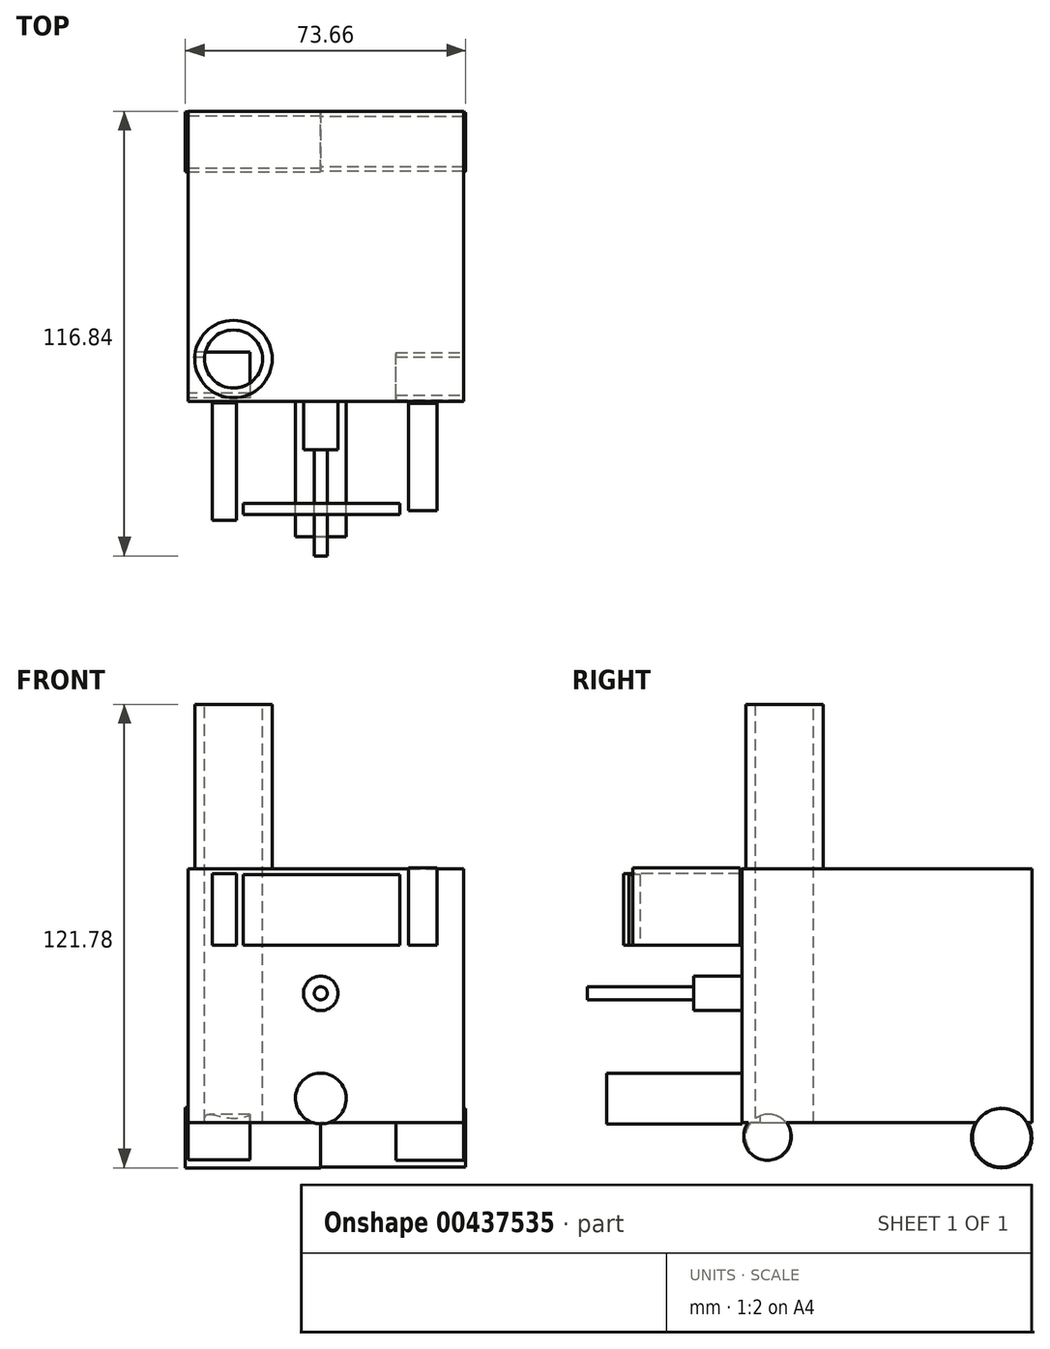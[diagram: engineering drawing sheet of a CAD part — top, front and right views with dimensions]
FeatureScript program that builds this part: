
annotation { "Feature Type Name" : "Feature", "Feature Type Description" : "" }
export const myFeature = defineFeature(function(context is Context, id is Id, definition is map)
    precondition{}
    {
        {
            var Q0;
            Q0=qCreatedBy(makeId("Front.planeOp"),FACE);
            var sketch = newSketch(context, id + "F0", { "sketchPlane" : qUnion([Q0])});
            skLineSegment(sketch, "E0.bottom", {"start": v(-34.88, -34.01) * mm, "end": v(37.54, -34.01) * mm});
            skLineSegment(sketch, "E0.top", {"start": v(-34.88, 32.75) * mm, "end": v(37.54, 32.75) * mm});
            skLineSegment(sketch, "E0.left", {"start": v(-34.88, -34.01) * mm, "end": v(-34.88, 32.75) * mm});
            skLineSegment(sketch, "E0.right", {"start": v(37.54, -34.01) * mm, "end": v(37.54, 32.75) * mm});
            skSolve(sketch);
        }
        {
            var Q0;
            Q0 = qSketchRegion(id + "F0", true);
            extrude(context, id + "F1", {"entities" : qUnion([Q0]), "depth" : 76.2 * mm});
        }
        {
            var Q0;
            Q0=makeQuery(id+"F1.opExtrude","SWEPT_FACE",FACE,{"disambiguationData":[OSD([sQuery(id+"F0.wireOp",EDGE,"E0.top")])]});
            var sketch = newSketch(context, id + "F2", { "sketchPlane" : qUnion([Q0])});
            skCircle(sketch, "E1", {"center": v(-22.93, -65.1) * mm, "radius": 10.17 * mm});
            skSolve(sketch);
        }
        {
            var Q0;
            Q0 = qSketchRegion(id + "F2", true);
            extrude(context, id + "F3", {"entities" : qUnion([Q0]), "operationType" : NewBodyOperationType.ADD, "depth" : 43.18 * mm});
        }
        {
            var Q0;
            Q0=makeQuery(id+"F1.opExtrude","CAP_FACE",FACE,{"disambiguationData":[OSD([sQuery(id+"F0.wireOp",EDGE,"E0.bottom"),sQuery(id+"F0.wireOp",EDGE,"E0.top"),sQuery(id+"F0.wireOp",EDGE,"E0.left"),sQuery(id+"F0.wireOp",EDGE,"E0.right")])],"isStart":false});
            var sketch = newSketch(context, id + "F4", { "sketchPlane" : qUnion([Q0])});
            skCircle(sketch, "E2", {"center": v(0, -27.64) * mm, "radius": 6.67 * mm});
            skSolve(sketch);
        }
        {
            var Q0;
            Q0 = qSketchRegion(id + "F4", true);
            extrude(context, id + "F5", {"entities" : qUnion([Q0]), "operationType" : NewBodyOperationType.ADD, "depth" : 35.56 * mm});
        }
        {
            var Q0;
            Q0=qCreatedBy(makeId("Right.planeOp"),FACE);
            var sketch = newSketch(context, id + "F6", { "sketchPlane" : qUnion([Q0])});
            skCircle(sketch, "E3", {"center": v(-8.03, -37.95) * mm, "radius": 7.71 * mm});
            skSolve(sketch);
        }
        {
            var Q0;
            Q0 = qSketchRegion(id + "F6", true);
            extrude(context, id + "F7", {"entities" : qUnion([Q0]), "operationType" : NewBodyOperationType.ADD, "depth" : 38.1 * mm});
        }
        {
            var Q0;
            Q0=makeQuery(id+"F7.opExtrude","CAP_FACE",FACE,{"disambiguationData":[OSD([sQuery(id+"F6.wireOp",EDGE,"E3")])],"isStart":true});
            var sketch = newSketch(context, id + "F8", { "sketchPlane" : qUnion([Q0])});
            skCircle(sketch, "E4", {"center": v(8.03, -37.95) * mm, "radius": 7.9 * mm});
            skSolve(sketch);
        }
        {
            var Q0;
            Q0 = qSketchRegion(id + "F8", true);
            extrude(context, id + "F9", {"entities" : qUnion([Q0]), "operationType" : NewBodyOperationType.ADD, "depth" : 35.56 * mm});
        }
        {
            var Q0;
            Q0=makeQuery(id+"F1.opExtrude","SWEPT_FACE",FACE,{"disambiguationData":[OSD([sQuery(id+"F0.wireOp",EDGE,"E0.right")])]});
            var sketch = newSketch(context, id + "F10", { "sketchPlane" : qUnion([Q0])});
            skCircle(sketch, "E5", {"center": v(-69.6, -37.64) * mm, "radius": 6.22 * mm});
            skSolve(sketch);
        }
        {
            var Q0;
            {var subQ0=sQuery(id+"F10.wireOp",EDGE,"E5");var subQ1=sQuery(id+"F0.wireOp",EDGE,"E0.bottom");var subQ2=sQuery(id+"F0.wireOp",EDGE,"E0.right");var subQ3=makeQuery(id+"F7.boolean.opBoolean","SPLIT",EDGE,{"disambiguationData":[TD([makeQuery(id+"F1.opExtrude","CAP_FACE",FACE,{"disambiguationData":[OSD([subQ1,sQuery(id+"F0.wireOp",EDGE,"E0.top"),sQuery(id+"F0.wireOp",EDGE,"E0.left"),subQ2])],"isStart":false})])],"derivedFrom":makeQuery(id+"F1.opExtrude","SWEPT_EDGE",EDGE,{"disambiguationData":[OSD([subQ1,subQ2])]})});var subQ4=makeQuery(id+"F10.imprint","INTERSECT",VERTEX,{"disambiguationData":[OD(0.0)],"derivedFrom":[subQ3,subQ0]});Q0=makeQuery(id+"F10.imprint","IMPRINT",FACE,{"disambiguationData":[TD([[makeQuery(id+"F10.imprint","IMPRINT",EDGE,{"disambiguationData":[TD([[subQ4,-1.0]])],"derivedFrom":subQ0}),1.0]])]});}
            extrude(context, id + "F11", {"entities" : qUnion([Q0]), "operationType" : NewBodyOperationType.ADD, "oppositeDirection" : true, "depth" : 17.78 * mm});
        }
        {
            var Q0;
            Q0=makeQuery(id+"F1.opExtrude","CAP_FACE",FACE,{"disambiguationData":[OSD([sQuery(id+"F0.wireOp",EDGE,"E0.bottom"),sQuery(id+"F0.wireOp",EDGE,"E0.top"),sQuery(id+"F0.wireOp",EDGE,"E0.left"),sQuery(id+"F0.wireOp",EDGE,"E0.right")])],"isStart":false});
            var sketch = newSketch(context, id + "F12", { "sketchPlane" : qUnion([Q0])});
            skPoint(sketch, "E6", {"position": v(0, -27.64) * mm});
            skSolve(sketch);
        }
        {
            var Q0;
            Q0=makeQuery(id+"F1.opExtrude","SWEPT_FACE",FACE,{"disambiguationData":[OSD([sQuery(id+"F0.wireOp",EDGE,"E0.left")])]});
            var sketch = newSketch(context, id + "F13", { "sketchPlane" : qUnion([Q0])});
            skCircle(sketch, "E7", {"center": v(69.44, -37.95) * mm, "radius": 6.17 * mm});
            skSolve(sketch);
        }
        {
            var Q0;
            {var subQ4=sQuery(id+"F0.wireOp",EDGE,"E0.top");Q0=makeQuery(id+"F12.imprint","IMPRINT",FACE,{"disambiguationData":[TD([[makeQuery(id+"F12.imprint","IMPRINT",EDGE,{"derivedFrom":makeQuery(id+"F1.opExtrude","CAP_EDGE",EDGE,{"disambiguationData":[OSD([subQ4])],"isStart":false})}),-1.0]])]});}
            var sketch = newSketch(context, id + "F14", { "sketchPlane" : qUnion([Q0])});
            skCircle(sketch, "E8", {"center": v(0, 0) * mm, "radius": 4.54 * mm});
            skSolve(sketch);
        }
        {
            var Q0;
            Q0 = qSketchRegion(id + "F14", true);
            extrude(context, id + "F15", {"entities" : qUnion([Q0]), "operationType" : NewBodyOperationType.ADD, "depth" : 12.7 * mm});
        }
        {
            var Q0;
            Q0=makeQuery(id+"F15.opExtrude","CAP_FACE",FACE,{"disambiguationData":[OSD([sQuery(id+"F14.wireOp",EDGE,"E8")])],"isStart":false});
            var sketch = newSketch(context, id + "F16", { "sketchPlane" : qUnion([Q0])});
            skCircle(sketch, "E9", {"center": v(0, 0) * mm, "radius": 3.21 * mm});
            skSolve(sketch);
        }
        {
            var Q0;
            {var subQ4=sQuery(id+"F0.wireOp",EDGE,"E0.top");Q0=makeQuery(id+"F12.imprint","IMPRINT",FACE,{"disambiguationData":[TD([[makeQuery(id+"F12.imprint","IMPRINT",EDGE,{"derivedFrom":makeQuery(id+"F1.opExtrude","CAP_EDGE",EDGE,{"disambiguationData":[OSD([subQ4])],"isStart":false})}),-1.0]])]});}
            var sketch = newSketch(context, id + "F17", { "sketchPlane" : qUnion([Q0])});
            skLineSegment(sketch, "E10", {"start": v(-28.64, 12.65) * mm, "end": v(32.01, 12.65) * mm});
            skSolve(sketch);
        }
        {
            var Q0;
            Q0 = qConstructionFilter(qBodyType(qCreatedBy(id + "F17" ,EDGE), BodyType.WIRE), ConstructionObject.NO);
            extrude(context, id + "F18", {"bodyType" : ToolBodyType.SURFACE, "surfaceEntities" : qUnion([Q0]), "depth" : 31.5 * mm});
        }
        {
            var Q0;
            Q0=makeQuery(id+"F18.opExtrude","SWEPT_FACE",FACE,{"disambiguationData":[OSD([sQuery(id+"F17.wireOp",EDGE,"E10")])]});
            var sketch = newSketch(context, id + "F19", { "sketchPlane" : qUnion([Q0])});
            skLineSegment(sketch, "E11", {"start": v(32.16, 107.3) * mm, "end": v(-28.8, 107.3) * mm});
            skSolve(sketch);
        }
        {
            var Q0;
            {var subQ5=makeQuery(id+"F18.opExtrude","CAP_EDGE",EDGE,{"disambiguationData":[OSD([sQuery(id+"F17.wireOp",EDGE,"E10")])],"isStart":true});Q0=makeQuery(id+"F19.imprint","IMPRINT",FACE,{"disambiguationData":[TD([[makeQuery(id+"F19.imprint","IMPRINT",EDGE,{"derivedFrom":subQ5}),1.0]])]});}
            var sketch = newSketch(context, id + "F20", { "sketchPlane" : qUnion([Q0])});
            skLineSegment(sketch, "E12.bottom", {"start": v(-22.18, 76.61) * mm, "end": v(-28.57, 76.61) * mm});
            skLineSegment(sketch, "E12.top", {"start": v(-22.18, 107.44) * mm, "end": v(-28.57, 107.44) * mm});
            skLineSegment(sketch, "E12.left", {"start": v(-22.18, 76.61) * mm, "end": v(-22.18, 107.44) * mm});
            skLineSegment(sketch, "E12.right", {"start": v(-28.57, 76.61) * mm, "end": v(-28.57, 107.44) * mm});
            skSolve(sketch);
        }
        {
            var Q0;
            Q0 = qSketchRegion(id + "F20", true);
            extrude(context, id + "F21", {"entities" : qUnion([Q0]), "oppositeDirection" : true, "depth" : 18.8 * mm});
        }
        {
            var Q0;
            {var subQ5=makeQuery(id+"F18.opExtrude","CAP_EDGE",EDGE,{"disambiguationData":[OSD([sQuery(id+"F17.wireOp",EDGE,"E10")])],"isStart":true});Q0=makeQuery(id+"F19.imprint","IMPRINT",FACE,{"disambiguationData":[TD([[makeQuery(id+"F19.imprint","IMPRINT",EDGE,{"derivedFrom":subQ5}),1.0]])]});}
            var sketch = newSketch(context, id + "F22", { "sketchPlane" : qUnion([Q0])});
            skLineSegment(sketch, "E13.bottom", {"start": v(30.6, 104.98) * mm, "end": v(23.05, 104.98) * mm});
            skLineSegment(sketch, "E13.top", {"start": v(30.6, 76.81) * mm, "end": v(23.05, 76.81) * mm});
            skLineSegment(sketch, "E13.left", {"start": v(30.6, 104.98) * mm, "end": v(30.6, 76.81) * mm});
            skLineSegment(sketch, "E13.right", {"start": v(23.05, 104.98) * mm, "end": v(23.05, 76.81) * mm});
            skSolve(sketch);
        }
        {
            var Q0;
            Q0 = qSketchRegion(id + "F22", true);
            extrude(context, id + "F23", {"entities" : qUnion([Q0]), "depth" : -20.32 * mm});
        }
        {
            var Q0;
            {var subQ5=makeQuery(id+"F18.opExtrude","CAP_EDGE",EDGE,{"disambiguationData":[OSD([sQuery(id+"F17.wireOp",EDGE,"E10")])],"isStart":true});Q0=makeQuery(id+"F19.imprint","IMPRINT",FACE,{"disambiguationData":[TD([[makeQuery(id+"F19.imprint","IMPRINT",EDGE,{"derivedFrom":subQ5}),1.0]])]});}
            var sketch = newSketch(context, id + "F24", { "sketchPlane" : qUnion([Q0])});
            skLineSegment(sketch, "E14.bottom", {"start": v(-20.44, 103.08) * mm, "end": v(20.75, 103.08) * mm});
            skLineSegment(sketch, "E14.top", {"start": v(-20.44, 106.02) * mm, "end": v(20.75, 106.02) * mm});
            skLineSegment(sketch, "E14.left", {"start": v(-20.44, 103.08) * mm, "end": v(-20.44, 106.02) * mm});
            skLineSegment(sketch, "E14.right", {"start": v(20.75, 103.08) * mm, "end": v(20.75, 106.02) * mm});
            skSolve(sketch);
        }
        {
            var Q0;
            Q0=makeQuery(id+"F24.imprint","IMPRINT",FACE,{"disambiguationData":[TD([[makeQuery(id+"F24.imprint","IMPRINT",EDGE,{"derivedFrom":sQuery(id+"F24.wireOp",EDGE,"E14.bottom")}),1.0]])]});
            extrude(context, id + "F25", {"entities" : qUnion([Q0]), "oppositeDirection" : true, "depth" : 18.54 * mm});
        }
        {
            var Q0;
            Q0=makeQuery(id+"F3.opExtrude","CAP_FACE",FACE,{"disambiguationData":[OSD([sQuery(id+"F2.wireOp",EDGE,"E1")])],"isStart":false});
            var sketch = newSketch(context, id + "F26", { "sketchPlane" : qUnion([Q0])});
            skPoint(sketch, "E15", {"position": v(-22.93, -65.1) * mm});
            skSolve(sketch);
        }
        {
            var Q0;
            Q0=sQuery(id+"F26.wireOp",VERTEX,"E15");
            var Q1;
            Q1=makeQuery(id+"F1.opExtrude","SWEPT_BODY",BODY,{"disambiguationData":[OSD([sQuery(id+"F0.wireOp",EDGE,"E0.bottom"),sQuery(id+"F0.wireOp",EDGE,"E0.top"),sQuery(id+"F0.wireOp",EDGE,"E0.left"),sQuery(id+"F0.wireOp",EDGE,"E0.right")])]});
            hole(context, id + "F27", {"style" : HoleStyle.SIMPLE, "endStyle" : HoleEndStyle.THROUGH, "holeDiameter" : 15.24 * mm, "isTappedThrough" : true, "tappedDepth" : 12.7 * mm, "tapClearance" : 3, "locations" : qUnion([Q0]), "scope" : qUnion([Q1])});
        }
        {
            var Q0;
            {var subQ0=sQuery(id+"F13.wireOp",EDGE,"E7");var subQ1=sQuery(id+"F0.wireOp",EDGE,"E0.bottom");var subQ2=sQuery(id+"F0.wireOp",EDGE,"E0.left");var subQ3=makeQuery(id+"F9.boolean.opBoolean","SPLIT",EDGE,{"disambiguationData":[TD([makeQuery(id+"F1.opExtrude","CAP_FACE",FACE,{"disambiguationData":[OSD([subQ1,sQuery(id+"F0.wireOp",EDGE,"E0.top"),subQ2,sQuery(id+"F0.wireOp",EDGE,"E0.right")])],"isStart":false})])],"derivedFrom":makeQuery(id+"F1.opExtrude","SWEPT_EDGE",EDGE,{"disambiguationData":[OSD([subQ1,subQ2])]})});var subQ4=makeQuery(id+"F13.imprint","INTERSECT",VERTEX,{"disambiguationData":[OD(0.0)],"derivedFrom":[subQ3,subQ0]});Q0=makeQuery(id+"F13.imprint","IMPRINT",FACE,{"disambiguationData":[TD([[makeQuery(id+"F13.imprint","IMPRINT",EDGE,{"disambiguationData":[TD([[subQ4,1.0]])],"derivedFrom":subQ0}),1.0]])]});}
            var sketch = newSketch(context, id + "F28", { "sketchPlane" : qUnion([Q0])});
            skCircle(sketch, "E16", {"center": v(69.34, -37.78) * mm, "radius": 6.01 * mm});
            skSolve(sketch);
        }
        {
            var Q0;
            Q0 = qSketchRegion(id + "F28", true);
            extrude(context, id + "F29", {"entities" : qUnion([Q0]), "operationType" : NewBodyOperationType.ADD, "oppositeDirection" : true, "depth" : 16.26 * mm});
        }
        {
            var Q0;
            Q0=makeQuery(id+"F16.imprint","IMPRINT",FACE,{"disambiguationData":[TD([[makeQuery(id+"F16.imprint","IMPRINT",EDGE,{"derivedFrom":sQuery(id+"F16.wireOp",EDGE,"E9")}),-1.0]])]});
            var sketch = newSketch(context, id + "F30", { "sketchPlane" : qUnion([Q0])});
            skCircle(sketch, "E17", {"center": v(0, 0) * mm, "radius": 1.7 * mm});
            skSolve(sketch);
        }
        {
            var Q0;
            Q0 = qSketchRegion(id + "F30", true);
            extrude(context, id + "F31", {"entities" : qUnion([Q0]), "operationType" : NewBodyOperationType.ADD, "depth" : 27.94 * mm});
        }
    });
